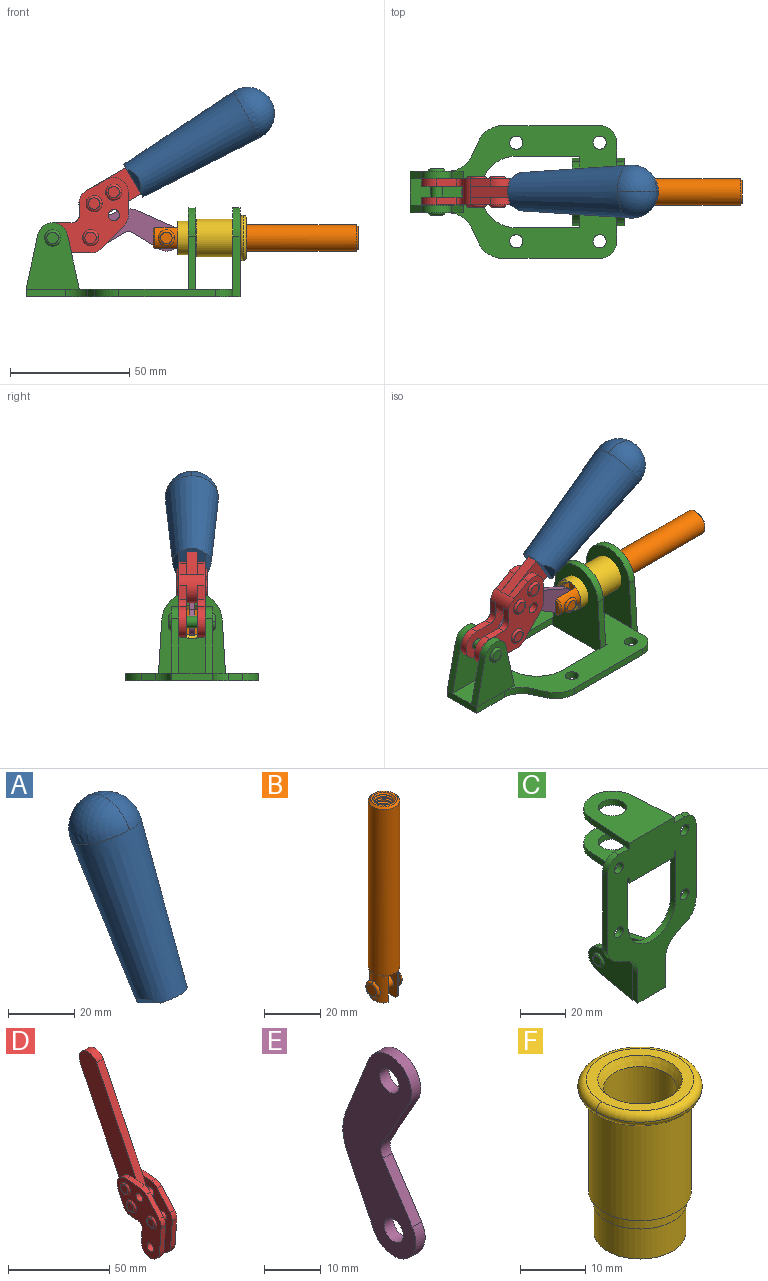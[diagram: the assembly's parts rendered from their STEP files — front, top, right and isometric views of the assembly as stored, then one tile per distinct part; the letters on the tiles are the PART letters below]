
ASSEMBLY  parts=6 mates=6
PART A: 11 faces, bbox 22.3x42.6x64.5 mm
  f0: sphere r=11.13mm, area 411.4mm2, adj f1,f8
  f1: cone r=11.11mm half-angle=3.3deg, axis (0,0.44,0.9), area 3251.8mm2, adj f0,f7,f8,f9,f10
  f2: cylinder r=6.16mm len=11.7mm, axis (1,0,0), area 89.5mm2, adj f3,f4,f5,f6
  f3: plane 60.23x36.75mm, normal (-1,0,0), area 763.6mm2, adj f2,f4,f6,f10
  f4: plane 51.37x25.05mm, normal (0,0.9,-0.44), area 264.2mm2, adj f2,f3,f5,f10
  f5: plane 60.23x36.75mm, normal (1,0,0), area 763.6mm2, adj f2,f4,f6,f10
  f6: plane 51.37x25.05mm, normal (0,-0.9,0.44), area 264.2mm2, adj f2,f3,f5,f10
  f7: plane 9.95x5.95mm, normal (0.71,-0.31,-0.64), area 25.8mm2, adj f1,f10
  f8: sphere r=11.13mm, area 411.4mm2, adj f0,f1
  f9: plane 9.95x5.95mm, normal (-0.71,-0.31,-0.64), area 25.8mm2, adj f1,f10
  f10: plane 14.27x11.38mm, normal (0,-0.44,-0.9), area 106.7mm2, adj f1,f3,f4,f5,f6,f7,f9
PART B: 48 faces, bbox 12.6x11.1x86.1 mm
  f0: torus R=2.41mm, axis (-1,0,0), area 15mm2, adj f30,f32,f34
  f1: torus R=2.41mm, axis (-1,0,0), area 15mm2, adj f29,f31,f33
  f2: cylinder r=5.54mm len=72.39mm, axis (0,0,1), area 2518.5mm2, adj f3,f4,f42,f43
  f3: cone r=5.54mm half-angle=45deg, axis (0,0,1), area 7.6mm2, adj f2,f5,f41
  f4: cone r=5.54mm half-angle=45deg, axis (0,0,-1), area 34.9mm2, adj f2,f39
  f5: cylinder r=5.08mm len=11.48mm, axis (0,0,1), area 108.3mm2, adj f3,f7,f8,f41
  f6: cylinder r=2.41mm len=4.83mm, axis (-1,0,0), area 71.2mm2, adj f40,f41
  f7: cylinder r=2.41mm len=4.83mm, axis (-1,0,0), area 7.6mm2, adj f5,f34
  f8: cone r=5.08mm half-angle=45deg, axis (0,0,1), area 10.6mm2, adj f5,f37,f41
  f9: cone r=3.98mm half-angle=45deg, axis (0,0,1), area 17.6mm2, adj f27,f39,f45,f46,f47
  f10: cylinder r=2.41mm len=4.83mm, axis (-1,0,0), area 7.6mm2, adj f33,f38
  f11: cylinder r=3.2mm len=6.4mm, axis (0,0,1), area 78.4mm2, adj f12,f28,f44,f45,f47
  f12: cylinder r=3.2mm len=6.4mm, axis (0,0,1), area 10.5mm2, adj f11,f13,f45,f47
  f13: cylinder r=3.2mm len=6.4mm, axis (0,0,1), area 10.5mm2, adj f12,f14,f45,f47
  f14: cylinder r=3.2mm len=6.4mm, axis (0,0,1), area 10.5mm2, adj f13,f15,f45,f47
  f15: cylinder r=3.2mm len=6.4mm, axis (0,0,1), area 10.5mm2, adj f14,f16,f45,f47
  f16: cylinder r=3.2mm len=6.4mm, axis (0,0,1), area 10.5mm2, adj f15,f17,f45,f47
  f17: cylinder r=3.2mm len=6.4mm, axis (0,0,1), area 10.5mm2, adj f16,f18,f45,f47
  f18: cylinder r=3.2mm len=6.4mm, axis (0,0,1), area 10.5mm2, adj f17,f19,f45,f47
  f19: cylinder r=3.2mm len=6.4mm, axis (0,0,1), area 10.5mm2, adj f18,f20,f45,f47
  f20: cylinder r=3.2mm len=6.4mm, axis (0,0,1), area 10.5mm2, adj f19,f21,f45,f47
  f21: cylinder r=3.2mm len=6.4mm, axis (0,0,1), area 10.5mm2, adj f20,f22,f45,f47
  f22: cylinder r=3.2mm len=6.4mm, axis (0,0,1), area 10.5mm2, adj f21,f23,f45,f47
  f23: cylinder r=3.2mm len=6.4mm, axis (0,0,1), area 10.5mm2, adj f22,f24,f45,f47
  f24: cylinder r=3.2mm len=6.4mm, axis (0,0,1), area 10.5mm2, adj f23,f25,f45,f47
  f25: cylinder r=3.2mm len=6.4mm, axis (0,0,1), area 10.5mm2, adj f24,f26,f45,f47
  f26: cylinder r=3.2mm len=6.4mm, axis (0,0,1), area 10.5mm2, adj f25,f27,f45,f47
  f27: cylinder r=3.2mm len=6.4mm, axis (0,0,1), area 7.4mm2, adj f9,f26,f45,f47
  f28: cone r=3.2mm half-angle=60deg, axis (0,0,1), area 37.2mm2, adj f11
  f29: plane 4.83x4.83mm, normal (-1,0,0), area 18.3mm2, adj f1,f31
  f30: plane 4.83x4.83mm, normal (1,0,0), area 18.3mm2, adj f0,f32
  f31: torus R=2.41mm, axis (-1,0,0), area 15mm2, adj f1,f29,f33
  f32: torus R=2.41mm, axis (-1,0,0), area 15mm2, adj f0,f30,f34
  f33: plane 6.83x6.83mm, normal (1,0,0), area 18.3mm2, adj f1,f10,f31
  f34: plane 6.83x6.83mm, normal (-1,0,0), area 18.3mm2, adj f0,f7,f32
  f35: cone r=5.08mm half-angle=45deg, axis (0,0,1), area 10.6mm2, adj f36,f38,f40
  f36: plane 7.25x1.97mm, normal (0,0,-1), area 10mm2, adj f35,f40
  f37: plane 7.25x1.97mm, normal (0,0,-1), area 10mm2, adj f8,f41
  f38: cylinder r=5.08mm len=11.48mm, axis (0,0,1), area 108.3mm2, adj f10,f35,f40,f42
  f39: plane 9.55x9.55mm, normal (0,0,1), area 22mm2, adj f4,f9
  f40: plane 12.76x10.09mm, normal (1,0,0), area 95.7mm2, adj f6,f35,f36,f38,f42,f43
  f41: plane 12.76x10.09mm, normal (-1,0,0), area 95.7mm2, adj f3,f5,f6,f8,f37,f43
  f42: cone r=5.54mm half-angle=45deg, axis (0,0,1), area 7.6mm2, adj f2,f38,f40
  f43: plane 11.07x4.7mm, normal (0,0,-1), area 50.4mm2, adj f2,f40,f41
  f44: plane 0.89x0.62mm, normal (-1,0,0), area 0.3mm2, adj f11,f45,f46,f47
  f45: bspline ~24.8x7.63mm, area 266.6mm2, adj f9,f11,f12,f13,f14,f15,f16,f17
  f46: bspline ~24.87x7.63mm, area 73.6mm2, adj f9,f44,f45,f47
  f47: bspline ~24.98x7.63mm, area 272.5mm2, adj f9,f11,f12,f13,f14,f15,f16,f17
PART C: 55 faces, bbox 55.7x37.4x89.8 mm
  f0: torus R=2.41mm, axis (-1,0,0), area 15mm2, adj f11,f15,f25
  f1: torus R=2.41mm, axis (-1,0,0), area 15mm2, adj f10,f12,f22
  f2: cylinder r=2.78mm len=5.56mm, axis (0,-1,0), area 54.2mm2, adj f30,f54
  f3: cylinder r=14.99mm len=29.97mm, axis (0,-1,0), area 145.9mm2, adj f30,f49,f53,f54
  f4: cylinder r=2.78mm len=5.56mm, axis (0,-1,0), area 54.2mm2, adj f30,f54
  f5: cylinder r=2.78mm len=5.56mm, axis (0,-1,0), area 54.2mm2, adj f30,f54
  f6: cylinder r=2.78mm len=5.56mm, axis (0,-1,0), area 54.2mm2, adj f30,f54
  f7: cylinder r=6.35mm len=12.7mm, axis (0,0,1), area 123.6mm2, adj f27,f51
  f8: cylinder r=6.35mm len=12.7mm, axis (0,0,-1), area 124.7mm2, adj f21,f35
  f9: cylinder r=2.41mm len=11.18mm, axis (-1,0,0), area 169.4mm2, adj f16,f19
  f10: plane 4.83x4.83mm, normal (1,0,0), area 18.3mm2, adj f1,f12
  f11: plane 4.83x4.83mm, normal (-1,0,0), area 18.3mm2, adj f0,f15
  f12: torus R=2.41mm, axis (-1,0,0), area 15mm2, adj f1,f10,f22
  f13: cylinder r=6.35mm len=12.41mm, axis (1,0,0), area 53.4mm2, adj f18,f19,f22,f23
  f14: cylinder r=6.35mm len=12.41mm, axis (-1,0,0), area 53.4mm2, adj f16,f17,f24,f25
  f15: torus R=2.41mm, axis (-1,0,0), area 15mm2, adj f0,f11,f25
  f16: plane 27.86x22.35mm, normal (1,0,0), area 425.4mm2, adj f9,f14,f17,f24,f30
  f17: plane 22.86x4.97mm, normal (0,0.21,0.98), area 72.5mm2, adj f14,f16,f25,f30
  f18: plane 22.86x4.97mm, normal (0,0.21,0.98), area 72.5mm2, adj f13,f19,f22,f30
  f19: plane 27.86x22.35mm, normal (-1,0,0), area 425.4mm2, adj f9,f13,f18,f23,f30
  f20: cylinder r=12.7mm len=25.35mm, axis (0,0,-1), area 119.8mm2, adj f21,f34,f35,f36
  f21: plane 34.21x28.07mm, normal (0,0,-1), area 702.4mm2, adj f8,f20,f30,f34,f36
  f22: plane 27.96x22.45mm, normal (1,0,0), area 407.2mm2, adj f1,f12,f13,f18,f23,f30,f42,f43
  f23: plane 22.86x4.97mm, normal (0,0.21,-0.98), area 72.5mm2, adj f13,f19,f22,f44
  f24: plane 22.86x4.97mm, normal (0,0.21,-0.98), area 72.5mm2, adj f14,f16,f25,f44
  f25: plane 27.86x22.35mm, normal (-1,0,0), area 407.1mm2, adj f0,f14,f15,f17,f24,f30,f45,f46
  f26: plane 3.1x0.95mm, normal (0,0,-1), area 2.7mm2, adj f30,f49,f50,f54
  f27: plane 34.21x28.07mm, normal (0,0,1), area 702.4mm2, adj f7,f28,f30,f50,f52
  f28: cylinder r=12.7mm len=25.35mm, axis (0,0,1), area 118.8mm2, adj f27,f50,f51,f52
  f29: plane 3.1x0.95mm, normal (0,0,-1), area 2.7mm2, adj f30,f52,f53,f54
  f30: plane 86.54x55.63mm, normal (0,1,0), area 2362.9mm2, adj f2,f3,f4,f5,f6,f16,f17,f18
  f31: plane 40.56x3.1mm, normal (-1,0,0), area 125.7mm2, adj f30,f32,f48,f54
  f32: cylinder r=7.11mm len=7.11mm, axis (0,-1,0), area 34.6mm2, adj f30,f31,f33,f54
  f33: plane 6.67x3.1mm, normal (0,0,1), area 20.4mm2, adj f30,f32,f34,f54
  f34: plane 25.39x3.13mm, normal (-1,0.06,0), area 79.5mm2, adj f20,f21,f33,f35,f54
  f35: plane 37.31x28.45mm, normal (0,0,1), area 789.9mm2, adj f8,f20,f34,f36,f54
  f36: plane 25.39x3.13mm, normal (1,0.06,0), area 79.5mm2, adj f20,f21,f35,f37,f54
  f37: plane 6.67x3.1mm, normal (0,0,1), area 20.4mm2, adj f30,f36,f38,f54
  f38: cylinder r=7.11mm len=7.11mm, axis (0,-1,0), area 34.6mm2, adj f30,f37,f39,f54
  f39: plane 40.56x3.1mm, normal (1,0,0), area 125.7mm2, adj f30,f38,f40,f54
  f40: cylinder r=11.18mm len=10.16mm, axis (0,-1,0), area 39.5mm2, adj f30,f39,f41,f54
  f41: plane 6.09x3.1mm, normal (0.42,0,-0.91), area 20.8mm2, adj f30,f40,f42,f54
  f42: cylinder r=11.18mm len=9.41mm, axis (0,-1,0), area 37.2mm2, adj f22,f30,f41,f43,f54
  f43: plane 16.5x3.1mm, normal (1,0,0), area 51.1mm2, adj f22,f42,f44,f54
  f44: plane 17.37x3.1mm, normal (0,0,-1), area 53.8mm2, adj f23,f24,f30,f43,f45,f54
  f45: plane 16.5x3.1mm, normal (-1,0,0), area 51.1mm2, adj f25,f44,f46,f54
  f46: cylinder r=11.18mm len=9.41mm, axis (0,-1,0), area 37.2mm2, adj f25,f30,f45,f47,f54
  f47: plane 6.09x3.1mm, normal (-0.42,0,-0.91), area 20.8mm2, adj f30,f46,f48,f54
  f48: cylinder r=11.18mm len=10.16mm, axis (0,-1,0), area 39.5mm2, adj f30,f31,f47,f54
  f49: plane 26.54x3.1mm, normal (-1,0,0), area 82.3mm2, adj f3,f26,f30,f54
  f50: plane 25.39x3.1mm, normal (1,0.06,0), area 78.8mm2, adj f26,f27,f28,f51,f54
  f51: plane 37.31x28.45mm, normal (0,0,-1), area 789.9mm2, adj f7,f28,f50,f52,f54
  f52: plane 25.39x3.1mm, normal (-1,0.06,0), area 78.8mm2, adj f27,f28,f29,f51,f54
  f53: plane 26.54x3.1mm, normal (1,0,0), area 82.3mm2, adj f3,f29,f30,f54
  f54: plane 89.66x55.63mm, normal (0,-1,0), area 2678.5mm2, adj f2,f3,f4,f5,f6,f26,f29,f31
PART D: 59 faces, bbox 12.9x60.2x99.6 mm
  f0: torus R=2.39mm, axis (-1,0,0), area 14.9mm2, adj f20,f43,f51
  f1: torus R=2.39mm, axis (-1,0,0), area 14.9mm2, adj f19,f42,f51
  f2: torus R=2.39mm, axis (-1,0,0), area 14.9mm2, adj f18,f35,f51
  f3: torus R=2.39mm, axis (-1,0,0), area 14.9mm2, adj f14,f17,f23
  f4: torus R=2.39mm, axis (-1,0,0), area 14.9mm2, adj f13,f16,f23
  f5: torus R=2.39mm, axis (-1,0,0), area 14.9mm2, adj f12,f15,f23
  f6: cylinder r=2.39mm len=4.78mm, axis (1,0,0), area 46.5mm2, adj f48,f50,f51
  f7: cylinder r=2.39mm len=4.78mm, axis (1,0,0), area 46.5mm2, adj f50,f51
  f8: cylinder r=6.35mm len=12.68mm, axis (1,0,0), area 61.8mm2, adj f38,f39,f50,f51
  f9: cylinder r=2.39mm len=4.78mm, axis (-1,0,0), area 70.5mm2, adj f46,f50
  f10: cylinder r=2.39mm len=4.78mm, axis (-1,0,0), area 46.5mm2, adj f23,f45,f46
  f11: cylinder r=2.39mm len=4.78mm, axis (-1,0,0), area 46.5mm2, adj f23,f46
  f12: plane 4.78x4.78mm, normal (1,0,0), area 17.9mm2, adj f5,f15
  f13: plane 4.78x4.78mm, normal (1,0,0), area 17.9mm2, adj f4,f16
  f14: plane 4.78x4.78mm, normal (1,0,0), area 17.9mm2, adj f3,f17
  f15: torus R=2.39mm, axis (-1,0,0), area 14.9mm2, adj f5,f12,f23
  f16: torus R=2.39mm, axis (-1,0,0), area 14.9mm2, adj f4,f13,f23
  f17: torus R=2.39mm, axis (-1,0,0), area 14.9mm2, adj f3,f14,f23
  f18: plane 4.78x4.78mm, normal (-1,0,0), area 17.9mm2, adj f2,f35
  f19: plane 4.78x4.78mm, normal (-1,0,0), area 17.9mm2, adj f1,f42
  f20: plane 4.78x4.78mm, normal (-1,0,0), area 17.9mm2, adj f0,f43
  f21: plane 2.26x0.2mm, normal (1,0,0), area 0.2mm2, adj f31,f44
  f22: plane 2.26x0.2mm, normal (-1,0,0), area 0.2mm2, adj f41,f44
  f23: plane 39.37x30.77mm, normal (1,0,0), area 565.5mm2, adj f3,f4,f5,f10,f11,f15,f16,f17
  f24: cylinder r=6.1mm len=4.15mm, axis (-1,0,0), area 14.7mm2, adj f23,f25,f32,f46
  f25: plane 10.25x9.01mm, normal (0,-0.75,0.66), area 42.3mm2, adj f23,f24,f26,f46
  f26: cylinder r=6.35mm len=4.64mm, axis (-1,0,0), area 15.6mm2, adj f23,f25,f27,f46
  f27: plane 15.84x3.1mm, normal (0,-1,-0.07), area 49.2mm2, adj f23,f26,f28,f46
  f28: cylinder r=6.35mm len=12.68mm, axis (-1,0,0), area 61.8mm2, adj f23,f27,f29,f46
  f29: plane 8.11x3.1mm, normal (0,1,0.07), area 25.2mm2, adj f23,f28,f30,f46
  f30: cylinder r=3.05mm len=3.25mm, axis (-1,0,0), area 14.8mm2, adj f23,f29,f31,f46
  f31: plane 5.99x3.1mm, normal (0,0.07,-1), area 18.6mm2, adj f21,f23,f30,f44,f46
  f32: plane 9.5x3.1mm, normal (0,-0.07,1), area 29.5mm2, adj f23,f24,f33,f46,f47
  f33: cylinder r=6.1mm len=8.63mm, axis (-1,0,0), area 39.1mm2, adj f23,f32,f34,f47
  f34: plane 8.65x3.96mm, normal (0,0.91,-0.42), area 29.5mm2, adj f23,f33,f44,f47
  f35: torus R=2.39mm, axis (-1,0,0), area 14.9mm2, adj f2,f18,f51
  f36: plane 10.25x9.01mm, normal (0,-0.75,0.66), area 42.3mm2, adj f37,f49,f50,f51
  f37: cylinder r=6.35mm len=4.64mm, axis (1,0,0), area 15.6mm2, adj f36,f38,f50,f51
  f38: plane 15.84x3.1mm, normal (0,-1,-0.07), area 49.2mm2, adj f8,f37,f50,f51
  f39: plane 8.11x3.1mm, normal (0,1,0.07), area 25.2mm2, adj f8,f40,f50,f51
  f40: cylinder r=3.05mm len=3.25mm, axis (1,0,0), area 14.8mm2, adj f39,f41,f50,f51
  f41: plane 5.99x3.1mm, normal (0,0.07,-1), area 18.6mm2, adj f22,f40,f44,f50,f51
  f42: torus R=2.39mm, axis (-1,0,0), area 14.9mm2, adj f1,f19,f51
  f43: torus R=2.39mm, axis (-1,0,0), area 14.9mm2, adj f0,f20,f51
  f44: cylinder r=6.35mm len=12.12mm, axis (-1,0,0), area 128.9mm2, adj f21,f22,f23,f31,f34,f41,f46,f47
  f45: plane 2.65x1.35mm, normal (1,0,0), area 1mm2, adj f10,f55
  f46: plane 39.08x20.42mm, normal (-1,0,0), area 412.5mm2, adj f9,f10,f11,f24,f25,f26,f27,f28
  f47: plane 77.62x39.82mm, normal (1,0,0), area 850mm2, adj f32,f33,f34,f44,f53,f54,f55
  f48: plane 2.65x1.35mm, normal (-1,0,0), area 1mm2, adj f6,f55
  f49: cylinder r=6.1mm len=4.15mm, axis (1,0,0), area 14.7mm2, adj f36,f50,f51,f56
  f50: plane 39.08x20.42mm, normal (1,0,0), area 412.5mm2, adj f6,f7,f8,f9,f36,f37,f38,f39
  f51: plane 39.37x30.77mm, normal (-1,0,0), area 565.5mm2, adj f0,f1,f2,f6,f7,f8,f35,f36
  f52: plane 8.65x3.96mm, normal (0,0.91,-0.42), area 29.5mm2, adj f44,f51,f57,f58
  f53: plane 68.49x33.4mm, normal (0,0.9,-0.44), area 358.1mm2, adj f44,f47,f54,f58
  f54: cylinder r=6.35mm len=12.06mm, axis (1,0,0), area 93.7mm2, adj f47,f53,f55,f58
  f55: plane 68.49x33.4mm, normal (0,-0.9,0.44), area 358.1mm2, adj f44,f45,f46,f47,f48,f50,f54,f58
  f56: plane 9.5x3.1mm, normal (0,-0.07,1), area 29.5mm2, adj f49,f50,f51,f57,f58
  f57: cylinder r=6.1mm len=8.63mm, axis (1,0,0), area 39.1mm2, adj f51,f52,f56,f58
  f58: plane 77.62x39.82mm, normal (-1,0,0), area 850mm2, adj f44,f52,f53,f54,f55,f56,f57
PART E: 12 faces, bbox 2.3x18.2x42.8 mm
  f0: cylinder r=2.4mm len=4.8mm, axis (1,0,0), area 34.9mm2, adj f4,f11
  f1: cylinder r=10.41mm len=8.47mm, axis (1,0,0), area 20.2mm2, adj f4,f9,f10,f11
  f2: cylinder r=3.05mm len=3.16mm, axis (1,0,0), area 7.7mm2, adj f4,f6,f7,f11
  f3: cylinder r=2.4mm len=4.8mm, axis (1,0,0), area 34.9mm2, adj f4,f11
  f4: plane 42.81x18.23mm, normal (-1,0,0), area 414.1mm2, adj f0,f1,f2,f3,f5,f6,f7,f8
  f5: cylinder r=5.54mm len=10.67mm, axis (1,0,0), area 41.8mm2, adj f4,f6,f10,f11
  f6: plane 11.66x6.53mm, normal (0,-0.87,-0.49), area 30.9mm2, adj f2,f4,f5,f11
  f7: plane 11.17x7.33mm, normal (0,-0.84,0.55), area 30.9mm2, adj f2,f4,f8,f11
  f8: cylinder r=5.54mm len=10.51mm, axis (1,0,0), area 41.8mm2, adj f4,f7,f9,f11
  f9: plane 13.67x6.67mm, normal (0,0.9,-0.44), area 35.1mm2, adj f1,f4,f8,f11
  f10: plane 14.1x5.7mm, normal (0,0.93,0.37), area 35.1mm2, adj f1,f4,f5,f11
  f11: plane 42.81x18.23mm, normal (1,0,0), area 414.1mm2, adj f0,f1,f2,f3,f5,f6,f7,f8
PART F: 15 faces, bbox 20.6x20.6x28.7 mm
  f0: torus R=8.26mm, axis (0,0,1), area 56.8mm2, adj f1,f10,f12
  f1: torus R=8.26mm, axis (0,0,1), area 56.8mm2, adj f0,f6,f13
  f2: cylinder r=5.59mm len=25.91mm, axis (0,0,1), area 909.6mm2, adj f3,f4
  f3: cone r=6.86mm half-angle=45deg, axis (0,0,-1), area 70.2mm2, adj f2,f14
  f4: cone r=6.47mm half-angle=30deg, axis (0,0,1), area 66.7mm2, adj f2,f13
  f5: cylinder r=7.04mm len=14.07mm, axis (0,0,1), area 252.6mm2, adj f11,f14
  f6: torus R=8.26mm, axis (0,0,1), area 56.8mm2, adj f1,f12,f13
  f7: cylinder r=7.16mm len=14.33mm, axis (0,0,1), area 91.5mm2, adj f9,f11
  f8: cylinder r=7.86mm len=18.42mm, axis (0,0,1), area 909.6mm2, adj f9,f10
  f9: plane 15.72x15.72mm, normal (0,0,-1), area 33mm2, adj f7,f8
  f10: plane 16.51x16.51mm, normal (0,0,-1), area 19.9mm2, adj f0,f8,f12
  f11: plane 14.33x14.33mm, normal (0,0,-1), area 5.7mm2, adj f5,f7
  f12: torus R=8.26mm, axis (0,0,1), area 56.8mm2, adj f0,f6,f10
  f13: plane 16.51x16.51mm, normal (0,0,1), area 82.7mm2, adj f1,f4,f6
  f14: plane 14.07x14.07mm, normal (0,0,-1), area 7.8mm2, adj f3,f5
PLACE A rot(axis=(0.56,0.56,0.61),117.6deg) t=(-7.68,0.04,2.47)mm
PLACE B rot(axis=(-0.58,0.58,-0.58),120deg) t=(-9.37,0,49.23)mm
PLACE C rot(axis=(0.58,0.58,0.58),120deg) t=(-9.43,0,0)mm fixed
PLACE D rot(axis=(0.56,0.56,0.61),117.6deg) t=(-7.68,0,2.47)mm
PLACE E rot(axis=(0.58,-0.58,-0.56),121.1deg) t=(-9.38,0,0.59)mm
PLACE F rot(axis=(0,1,0),90deg) t=(-9.43,-24.61,24.61)mm
MATE revolute D.f4 <-> E.f5  axis (0,-1,0) through (-25.65,0,24.69)mm
MATE revolute E.f3 <-> B.f6  axis (0,-1,0) through (6.1,0,24.61)mm
MATE cylindrical F.f2 <-> B.f2  axis (1,0,0) through (39.5,0,24.61)mm
MATE fastened A.f2 <-> D.f54  axis (0,-1,0) through (41.63,2.35,77.4)mm
MATE fastened F.f2 <-> C.f7  axis (-1,0,0) through (36.96,0,24.61)mm
MATE revolute D.f7 <-> C.f0  axis (0,1,0) through (-41.52,0,24.61)mm
